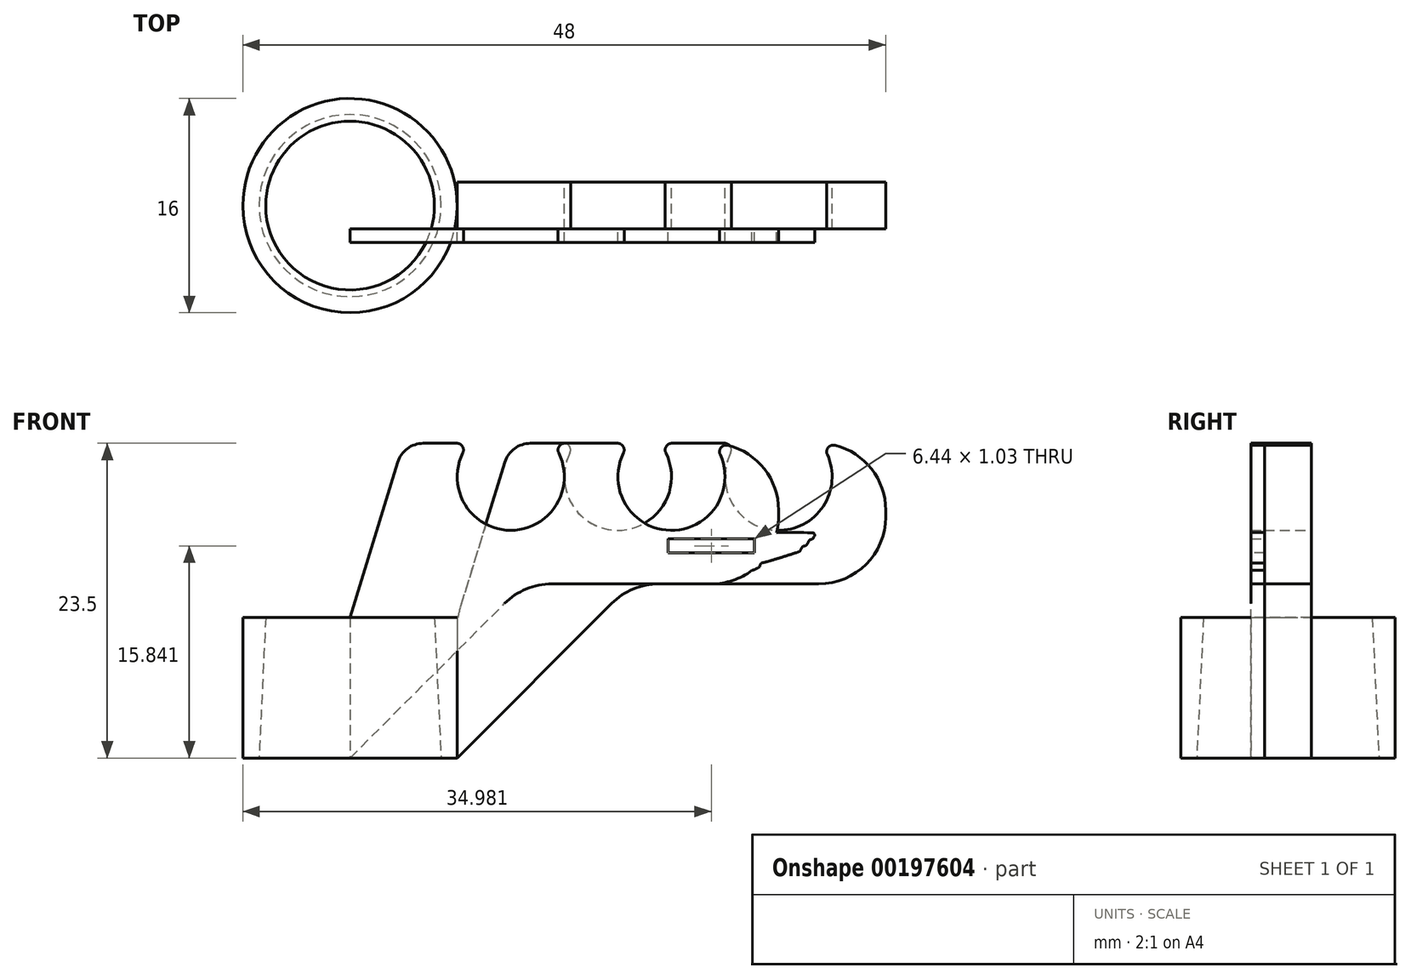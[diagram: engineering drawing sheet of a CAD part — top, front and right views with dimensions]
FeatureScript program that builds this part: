
annotation { "Feature Type Name" : "Feature", "Feature Type Description" : "" }
export const myFeature = defineFeature(function(context is Context, id is Id, definition is map)
    precondition{}
    {
        {
            var Q0;
            Q0=qCreatedBy(makeId("Top.planeOp"),FACE);
            var sketch = newSketch(context, id + "F0", { "sketchPlane" : qUnion([Q0])});
            skCircle(sketch, "E0", {"center": v(0, 0) * mm, "radius": 6.3 * mm});
            skCircle(sketch, "E1", {"center": v(0, 0) * mm, "radius": 8 * mm});
            skCircle(sketch, "E2", {"center": v(0, 0) * mm, "radius": 6.8 * mm});
            skSolve(sketch);
        }
        {
            var Q0;
            Q0=qCreatedBy(makeId("Front.planeOp"),FACE);
            var sketch = newSketch(context, id + "F1", { "sketchPlane" : qUnion([Q0])});
            skLineSegment(sketch, "E3.0", {"start": v(-6.8, 0) * mm, "end": v(6.8, 0) * mm});
            skLineSegment(sketch, "E4.0", {"start": v(-6.3, 0) * mm, "end": v(6.3, 0) * mm});
            skLineSegment(sketch, "E5.0", {"start": v(-8, 0) * mm, "end": v(-5.58, 0) * mm});
            skLineSegment(sketch, "E6", {"start": v(0, 0) * mm, "end": v(0, 10.5) * mm});
            skLineSegment(sketch, "E7.top", {"start": v(-8, 10.5) * mm, "end": v(-6.3, 10.5) * mm});
            skLineSegment(sketch, "E7.left", {"start": v(-8, 0) * mm, "end": v(-8, 10.5) * mm});
            skLineSegment(sketch, "E8", {"start": v(-6.3, 10.5) * mm, "end": v(-6.8, 0) * mm});
            skLineSegment(sketch, "E9.trimOffspring", {"start": v(0, 0) * mm, "end": v(8, 0) * mm});
            skSolve(sketch);
        }
        {
            var Q0;
            Q0=makeQuery(id+"F1.imprint","IMPRINT",FACE,{"disambiguationData":[TD([[makeQuery(id+"F1.imprint","IMPRINT",EDGE,{"derivedFrom":sQuery(id+"F1.wireOp",EDGE,"E7.top")}),-1.0]])]});
            var Q1;
            Q1=sQuery(id+"F1.wireOp",EDGE,"E6");
            revolve(context, id + "F2", {"entities" : qUnion([Q0]), "axis" : qUnion([Q1]), "revolveType" : RevolveType.FULL});
        }
        {
            var Q0;
            Q0=qCreatedBy(makeId("Front.planeOp"),FACE);
            var sketch = newSketch(context, id + "F3", { "sketchPlane" : qUnion([Q0])});
            skLineSegment(sketch, "E10", {"start": v(8, 10.5) * mm, "end": v(8, 0) * mm});
            skLineSegment(sketch, "E11.0", {"start": v(8, 10.5) * mm, "end": v(-8, 10.5) * mm});
            skLineSegment(sketch, "E12.0", {"start": v(-8, 0) * mm, "end": v(8, 0) * mm});
            skLineSegment(sketch, "E13", {"start": v(0, 13) * mm, "end": v(41.13, 13) * mm, "construction": true});
            skLineSegment(sketch, "E14", {"start": v(0, 21) * mm, "end": v(40.48, 21) * mm, "construction": true});
            skLineSegment(sketch, "E15", {"start": v(20, 25.73) * mm, "end": v(20, 4.34) * mm, "construction": true});
            skCircle(sketch, "E16", {"center": v(20, 21) * mm, "radius": 4 * mm});
            skCircle(sketch, "E17.1.0.0", {"center": v(32, 21) * mm, "radius": 4 * mm});
            skLineSegment(sketch, "E17.direction1", {"start": v(20, 21) * mm, "end": v(32, 21) * mm, "construction": true});
            skLineSegment(sketch, "E18", {"start": v(12, 25.64) * mm, "end": v(12, 16.43) * mm, "construction": true});
            skLineSegment(sketch, "E19", {"start": v(12, 23.5) * mm, "end": v(68.02, 23.5) * mm});
            skLineSegment(sketch, "E20", {"start": v(40, 26.61) * mm, "end": v(40, 15.45) * mm, "construction": true});
            skLineSegment(sketch, "E21", {"start": v(12, 23.5) * mm, "end": v(8, 10.5) * mm});
            skLineSegment(sketch, "E22", {"start": v(22.25, 13) * mm, "end": v(41.13, 13) * mm});
            skLineSegment(sketch, "E23", {"start": v(40, 13) * mm, "end": v(40, 23.5) * mm});
            skLineSegment(sketch, "E24", {"start": v(8, 0) * mm, "end": v(21, 13) * mm});
            skPoint(sketch, "E25.orphan", {"position": v(22.25, 14.25) * mm});
            skLineSegment(sketch, "E26", {"start": v(21, 13) * mm, "end": v(22.25, 13) * mm});
            skLineSegment(sketch, "E27", {"start": v(40, 13) * mm, "end": v(41.13, 13) * mm});
            skLineSegment(sketch, "E28.bottom", {"start": v(8, 10.5) * mm, "end": v(7.8, 10.5) * mm});
            skLineSegment(sketch, "E28.top", {"start": v(8, 0) * mm, "end": v(7.8, 0) * mm});
            skLineSegment(sketch, "E28.right", {"start": v(7.8, 10.5) * mm, "end": v(7.8, 0) * mm});
            skSolve(sketch);
        }
        {
            var Q0;
            {var subQ0=sQuery(id+"F3.wireOp",EDGE,"E21");Q0=makeQuery(id+"F3.imprint","IMPRINT",FACE,{"disambiguationData":[TD([[makeQuery(id+"F3.imprint","IMPRINT",EDGE,{"derivedFrom":subQ0}),1.0]])]});}
            var Q1;
            Q1=makeQuery(id+"F3.imprint","IMPRINT",FACE,{"disambiguationData":[TD([[makeQuery(id+"F3.imprint","IMPRINT",EDGE,{"derivedFrom":sQuery(id+"F3.wireOp",EDGE,"E28.bottom")}),1.0]])]});
            extrude(context, id + "F4", {"entities" : qUnion([Q0, Q1]), "operationType" : NewBodyOperationType.ADD, "endBound" : BoundingType.SYMMETRIC, "depth" : 3.5 * mm});
        }
        {
            var Q0;
            Q0=makeQuery(id+"F4.boolean.opBoolean","INTERSECT",EDGE,{"derivedFrom":[makeQuery(id+"F2.opRevolve","SWEPT_FACE",FACE,{"disambiguationData":[OSD([sQuery(id+"F1.wireOp",EDGE,"E7.left")])]}),makeQuery(id+"F4.opExtrude","CAP_FACE",FACE,{"disambiguationData":[OSD([sQuery(id+"F3.wireOp",EDGE,"E16"),sQuery(id+"F3.wireOp",EDGE,"E17.1.0.0"),sQuery(id+"F3.wireOp",EDGE,"E17.2.0.0"),sQuery(id+"F3.wireOp",EDGE,"E17.3.0.0"),sQuery(id+"F3.wireOp",EDGE,"E19"),sQuery(id+"F3.wireOp",EDGE,"E21"),sQuery(id+"F3.wireOp",EDGE,"E22"),sQuery(id+"F3.wireOp",EDGE,"E23"),sQuery(id+"F3.wireOp",EDGE,"E24"),sQuery(id+"F3.wireOp",EDGE,"E26"),sQuery(id+"F3.wireOp",EDGE,"E27"),sQuery(id+"F3.wireOp",EDGE,"E28.bottom"),sQuery(id+"F3.wireOp",EDGE,"E28.top"),sQuery(id+"F3.wireOp",EDGE,"E28.right")])],"isStart":true})]});
            var Q1;
            Q1=makeQuery(id+"F4.boolean.opBoolean","INTERSECT",EDGE,{"derivedFrom":[makeQuery(id+"F2.opRevolve","SWEPT_FACE",FACE,{"disambiguationData":[OSD([sQuery(id+"F1.wireOp",EDGE,"E7.left")])]}),makeQuery(id+"F4.opExtrude","CAP_FACE",FACE,{"disambiguationData":[OSD([sQuery(id+"F3.wireOp",EDGE,"E16"),sQuery(id+"F3.wireOp",EDGE,"E17.1.0.0"),sQuery(id+"F3.wireOp",EDGE,"E17.2.0.0"),sQuery(id+"F3.wireOp",EDGE,"E17.3.0.0"),sQuery(id+"F3.wireOp",EDGE,"E19"),sQuery(id+"F3.wireOp",EDGE,"E21"),sQuery(id+"F3.wireOp",EDGE,"E22"),sQuery(id+"F3.wireOp",EDGE,"E23"),sQuery(id+"F3.wireOp",EDGE,"E24"),sQuery(id+"F3.wireOp",EDGE,"E26"),sQuery(id+"F3.wireOp",EDGE,"E27"),sQuery(id+"F3.wireOp",EDGE,"E28.bottom"),sQuery(id+"F3.wireOp",EDGE,"E28.top"),sQuery(id+"F3.wireOp",EDGE,"E28.right")])],"isStart":false})]});
            var Q2;
            Q2=makeQuery(id+"F4.opExtrude","SWEPT_EDGE",EDGE,{"disambiguationData":[OSD([sQuery(id+"F3.wireOp",EDGE,"E24"),sQuery(id+"F3.wireOp",EDGE,"E26")])]});
            var Q3;
            Q3=makeQuery(id+"F4.opExtrude","SWEPT_EDGE",EDGE,{"disambiguationData":[OSD([sQuery(id+"F3.wireOp",EDGE,"E23"),sQuery(id+"F3.wireOp",EDGE,"E27")])]});
            fillet(context, id + "F5", {"entities" : qUnion([Q0, Q1, Q2, Q3]), "radius" : 5 * mm, "tangentPropagation" : true, "allowEdgeOverflow" : false});
        }
        {
            var Q0;
            Q0=makeQuery(id+"F4.opExtrude","SWEPT_EDGE",EDGE,{"disambiguationData":[OSD([sQuery(id+"F3.wireOp",EDGE,"E19"),sQuery(id+"F3.wireOp",EDGE,"E21")])]});
            var Q1;
            Q1=makeQuery(id+"F4.opExtrude","SWEPT_EDGE",EDGE,{"disambiguationData":[OSD([sQuery(id+"F3.wireOp",EDGE,"E19"),sQuery(id+"F3.wireOp",EDGE,"E23")])]});
            fillet(context, id + "F6", {"entities" : qUnion([Q0, Q1]), "radius" : 2 * mm, "tangentPropagation" : true, "allowEdgeOverflow" : false});
        }
        {
            var Q0;
            {var subQ0=sQuery(id+"F3.wireOp",EDGE,"E19");var subQ1=sQuery(id+"F3.wireOp",EDGE,"E16");Q0=makeQuery(id+"F4.opExtrude","SWEPT_EDGE",EDGE,{"disambiguationData":[OSD([subQ1,subQ0]),TDD([makeQuery(id+"F3.imprint","INTERSECT",VERTEX,{"disambiguationData":[OD(1.0)],"derivedFrom":[subQ1,subQ0]})])]});}
            var Q1;
            {var subQ0=sQuery(id+"F3.wireOp",EDGE,"E19");var subQ1=sQuery(id+"F3.wireOp",EDGE,"E16");Q1=makeQuery(id+"F4.opExtrude","SWEPT_EDGE",EDGE,{"disambiguationData":[OSD([subQ1,subQ0]),TDD([makeQuery(id+"F3.imprint","INTERSECT",VERTEX,{"disambiguationData":[OD(0.0)],"derivedFrom":[subQ1,subQ0]})])]});}
            var Q2;
            {var subQ0=sQuery(id+"F3.wireOp",EDGE,"E19");var subQ1=sQuery(id+"F3.wireOp",EDGE,"E17.1.0.0");Q2=makeQuery(id+"F4.opExtrude","SWEPT_EDGE",EDGE,{"disambiguationData":[OSD([subQ1,subQ0]),TDD([makeQuery(id+"F3.imprint","INTERSECT",VERTEX,{"disambiguationData":[OD(0.0)],"derivedFrom":[subQ1,subQ0]})])]});}
            var Q3;
            {var subQ0=sQuery(id+"F3.wireOp",EDGE,"E19");var subQ1=sQuery(id+"F3.wireOp",EDGE,"E17.2.0.0");Q3=makeQuery(id+"F4.opExtrude","SWEPT_EDGE",EDGE,{"disambiguationData":[OSD([subQ1,subQ0]),TDD([makeQuery(id+"F3.imprint","INTERSECT",VERTEX,{"disambiguationData":[OD(0.0)],"derivedFrom":[subQ1,subQ0]})])]});}
            var Q4;
            {var subQ0=sQuery(id+"F3.wireOp",EDGE,"E19");var subQ1=sQuery(id+"F3.wireOp",EDGE,"E17.3.0.0");Q4=makeQuery(id+"F4.opExtrude","SWEPT_EDGE",EDGE,{"disambiguationData":[OSD([subQ1,subQ0]),TDD([makeQuery(id+"F3.imprint","INTERSECT",VERTEX,{"disambiguationData":[OD(0.0)],"derivedFrom":[subQ1,subQ0]})])]});}
            var Q5;
            {var subQ0=sQuery(id+"F3.wireOp",EDGE,"E19");var subQ1=sQuery(id+"F3.wireOp",EDGE,"E17.1.0.0");Q5=makeQuery(id+"F4.opExtrude","SWEPT_EDGE",EDGE,{"disambiguationData":[OSD([subQ1,subQ0]),TDD([makeQuery(id+"F3.imprint","INTERSECT",VERTEX,{"disambiguationData":[OD(1.0)],"derivedFrom":[subQ1,subQ0]})])]});}
            var Q6;
            {var subQ0=sQuery(id+"F3.wireOp",EDGE,"E19");var subQ1=sQuery(id+"F3.wireOp",EDGE,"E17.2.0.0");Q6=makeQuery(id+"F4.opExtrude","SWEPT_EDGE",EDGE,{"disambiguationData":[OSD([subQ1,subQ0]),TDD([makeQuery(id+"F3.imprint","INTERSECT",VERTEX,{"disambiguationData":[OD(1.0)],"derivedFrom":[subQ1,subQ0]})])]});}
            var Q7;
            {var subQ0=sQuery(id+"F3.wireOp",EDGE,"E19");var subQ1=sQuery(id+"F3.wireOp",EDGE,"E17.3.0.0");Q7=makeQuery(id+"F4.opExtrude","SWEPT_EDGE",EDGE,{"disambiguationData":[OSD([subQ1,subQ0]),TDD([makeQuery(id+"F3.imprint","INTERSECT",VERTEX,{"disambiguationData":[OD(1.0)],"derivedFrom":[subQ1,subQ0]})])]});}
            var Q8;
            Q8=makeQuery(id+"F5.opFillet","BLEND_EDGE",EDGE,{"blendedFrom":[makeQuery(id+"F4.opExtrude","SWEPT_EDGE",EDGE,{"disambiguationData":[OSD([sQuery(id+"F3.wireOp",EDGE,"E19"),sQuery(id+"F3.wireOp",EDGE,"E23")])]}),makeQuery(id+"F4.opExtrude","SWEPT_FACE",FACE,{"disambiguationData":[OSD([sQuery(id+"F3.wireOp",EDGE,"E17.1.0.0")])]})],"blendedInto":[makeQuery(id+"F4.opExtrude","SWEPT_FACE",FACE,{"disambiguationData":[OSD([sQuery(id+"F3.wireOp",EDGE,"E17.1.0.0")])]})]});
            fillet(context, id + "F7", {"entities" : qUnion([Q0, Q1, Q2, Q3, Q4, Q5, Q6, Q7, Q8]), "radius" : .5 * mm, "tangentPropagation" : true, "allowEdgeOverflow" : false});
        }
        {
            var Q0;
            Q0=makeQuery(id+"F4.opExtrude","CAP_FACE",FACE,{"disambiguationData":[OSD([sQuery(id+"F3.wireOp",EDGE,"E16"),sQuery(id+"F3.wireOp",EDGE,"E17.1.0.0"),sQuery(id+"F3.wireOp",EDGE,"E17.2.0.0"),sQuery(id+"F3.wireOp",EDGE,"E17.3.0.0"),sQuery(id+"F3.wireOp",EDGE,"E19"),sQuery(id+"F3.wireOp",EDGE,"E21"),sQuery(id+"F3.wireOp",EDGE,"E22"),sQuery(id+"F3.wireOp",EDGE,"E23"),sQuery(id+"F3.wireOp",EDGE,"E24"),sQuery(id+"F3.wireOp",EDGE,"E26"),sQuery(id+"F3.wireOp",EDGE,"E27"),sQuery(id+"F3.wireOp",EDGE,"E28.bottom"),sQuery(id+"F3.wireOp",EDGE,"E28.top"),sQuery(id+"F3.wireOp",EDGE,"E28.right")])],"isStart":false});
            var sketch = newSketch(context, id + "F8", { "sketchPlane" : qUnion([Q0])});
            skFitSpline(sketch, "E29", {"points": [v(35.71, 16.35) * mm, v(35.78, 16.55) * mm, v(35.85, 16.65) * mm, v(35.98, 16.75) * mm, v(36.12, 16.8) * mm, v(36.24, 16.8) * mm, v(42.55, 16.82) * mm, v(42.65, 16.78) * mm, v(42.7, 16.65) * mm, v(42.65, 16.52) * mm, v(42.55, 16.36) * mm, v(42.42, 16.32) * mm, v(42.3, 16.26) * mm, v(42.08, 15.9) * mm, v(41.89, 15.83) * mm, v(41.78, 15.76) * mm, v(41.62, 15.48) * mm, v(41.45, 15.38) * mm, v(38.77, 14.57) * mm, v(38.7, 14.56) * mm, v(38.62, 14.38) * mm, v(38.56, 14.27) * mm, v(38.18, 14.06) * mm, v(38.06, 14.02) * mm, v(35.9, 13.44) * mm, v(35.75, 13.44) * mm, v(35.65, 13.48) * mm, v(35.59, 13.53) * mm, v(35, 14.06) * mm, v(34.97, 14.05) * mm, v(34.9, 14.03) * mm, v(34.85, 14) * mm, v(34.31, 13.47) * mm, v(34.24, 13.44) * mm, v(34.16, 13.44) * mm, v(31.77, 14.07) * mm, v(31.41, 14.28) * mm, v(31.3, 14.48) * mm, v(31.22, 14.57) * mm, v(31.12, 14.6) * mm, v(28.44, 15.4) * mm, v(28.33, 15.52) * mm, v(28.2, 15.88) * mm, v(28.14, 15.83) * mm, v(28.02, 15.85) * mm, v(27.94, 15.87) * mm, v(27.88, 15.92) * mm, v(27.69, 16.27) * mm, v(27.65, 16.3) * mm, v(27.51, 16.3) * mm, v(27.46, 16.32) * mm, v(27.28, 16.62) * mm, v(27.28, 16.7) * mm, v(27.33, 16.77) * mm, v(27.4, 16.8) * mm, v(27.46, 16.8) * mm, v(33.8, 16.81) * mm, v(33.85, 16.81) * mm, v(33.97, 16.77) * mm, v(34.17, 16.6) * mm, v(34.2, 16.5) * mm, v(34.25, 16.4) * mm, v(34.26, 16.34) * mm, v(34.33, 16.34) * mm, v(35.58, 16.34) * mm, v(35.71, 16.35) * mm]});
            skFitSpline(sketch, "E30", {"points": [v(30.68, 16.8) * mm, v(30.83, 16.69) * mm, v(30.9, 16.62) * mm, v(30.99, 16.5) * mm, v(31.06, 16.33) * mm, v(31.28, 16.02) * mm, v(31.53, 15.67) * mm, v(31.6, 15.6) * mm, v(32.13, 15.09) * mm, v(32.73, 14.67) * mm, v(33.36, 14.37) * mm, v(33.87, 14.2) * mm, v(34.55, 14.1) * mm, v(35, 14.06) * mm, v(35.61, 14.1) * mm, v(36.24, 14.24) * mm, v(36.81, 14.44) * mm, v(37.3, 14.7) * mm, v(37.8, 15.05) * mm, v(38.1, 15.33) * mm, v(38.48, 15.75) * mm, v(38.72, 16.05) * mm, v(38.93, 16.39) * mm, v(39.08, 16.63) * mm, v(39.22, 16.76) * mm, v(39.4, 16.82) * mm, v(39.46, 16.82) * mm], "startDerivative": vector(6.61, -4.14) * mm, "endDerivative": vector(2.94, -0.27) * mm});
            skLineSegment(sketch, "E31.bottom", {"start": v(31.76, 16.35) * mm, "end": v(38.2, 16.35) * mm});
            skLineSegment(sketch, "E31.top", {"start": v(31.76, 15.33) * mm, "end": v(38.2, 15.33) * mm});
            skLineSegment(sketch, "E31.left", {"start": v(31.76, 16.35) * mm, "end": v(31.76, 15.33) * mm});
            skLineSegment(sketch, "E31.right", {"start": v(38.2, 16.35) * mm, "end": v(38.2, 15.33) * mm});
            skLineSegment(sketch, "E32", {"start": v(27.69, 16.27) * mm, "end": v(31.76, 16.35) * mm});
            skLineSegment(sketch, "E33", {"start": v(31.76, 16.1) * mm, "end": v(28.2, 15.88) * mm});
            skLineSegment(sketch, "E34", {"start": v(31.76, 15.88) * mm, "end": v(28.44, 15.4) * mm});
            skLineSegment(sketch, "E35", {"start": v(31.76, 15.67) * mm, "end": v(29.25, 15.15) * mm});
            skLineSegment(sketch, "E36", {"start": v(31.76, 15.33) * mm, "end": v(30.28, 14.84) * mm});
            skLineSegment(sketch, "E37", {"start": v(32.82, 15.33) * mm, "end": v(31.22, 14.57) * mm});
            skLineSegment(sketch, "E38", {"start": v(33.59, 15.33) * mm, "end": v(31.77, 14.07) * mm});
            skLineSegment(sketch, "E39", {"start": v(34.05, 15.33) * mm, "end": v(32.59, 13.83) * mm});
            skLineSegment(sketch, "E40", {"start": v(34.4, 15.33) * mm, "end": v(33.39, 13.61) * mm});
            skLineSegment(sketch, "E41", {"start": v(34.73, 15.33) * mm, "end": v(34.16, 13.44) * mm});
            skLineSegment(sketch, "E42", {"start": v(34.98, 15.33) * mm, "end": v(34.97, 14.05) * mm});
            skLineSegment(sketch, "E43", {"start": v(35.26, 15.33) * mm, "end": v(35.81, 13.43) * mm});
            skLineSegment(sketch, "E44", {"start": v(35.61, 15.33) * mm, "end": v(36.58, 13.6) * mm});
            skLineSegment(sketch, "E45", {"start": v(35.96, 15.33) * mm, "end": v(37.37, 13.83) * mm});
            skLineSegment(sketch, "E46", {"start": v(36.38, 15.33) * mm, "end": v(38.18, 14.06) * mm});
            skLineSegment(sketch, "E47", {"start": v(37.14, 15.33) * mm, "end": v(38.77, 14.57) * mm});
            skLineSegment(sketch, "E48", {"start": v(38.2, 15.33) * mm, "end": v(39.77, 14.85) * mm});
            skLineSegment(sketch, "E49", {"start": v(38.2, 15.65) * mm, "end": v(40.68, 15.13) * mm});
            skLineSegment(sketch, "E50", {"start": v(38.2, 15.87) * mm, "end": v(41.57, 15.43) * mm});
            skLineSegment(sketch, "E51", {"start": v(38.2, 16.1) * mm, "end": v(42.02, 15.86) * mm});
            skLineSegment(sketch, "E52", {"start": v(38.2, 16.3) * mm, "end": v(42.35, 16.3) * mm});
            skSolve(sketch);
        }
        {
            var Q0;
            {var subQ5=sQuery(id+"F8.wireOp",EDGE,"E36");Q0=makeQuery(id+"F8.imprint","IMPRINT",FACE,{"disambiguationData":[TD([[makeQuery(id+"F8.imprint","IMPRINT",EDGE,{"derivedFrom":subQ5}),-1.0]])]});}
            var Q1;
            {var subQ0=sQuery(id+"F8.wireOp",EDGE,"E46");var subQ1=sQuery(id+"F8.wireOp",EDGE,"E29");var subQ2=makeQuery(id+"F8.imprint","INTERSECT",VERTEX,{"derivedFrom":[subQ1,subQ0]});Q1=makeQuery(id+"F8.imprint","IMPRINT",FACE,{"disambiguationData":[TD([[makeQuery(id+"F8.imprint","IMPRINT",EDGE,{"disambiguationData":[TD([[subQ2,1.0]])],"derivedFrom":subQ1}),-1.0]])]});}
            var Q2;
            {var subQ0=sQuery(id+"F8.wireOp",EDGE,"E38");var subQ1=sQuery(id+"F8.wireOp",EDGE,"E29");var subQ2=makeQuery(id+"F8.imprint","INTERSECT",VERTEX,{"derivedFrom":[subQ1,subQ0]});Q2=makeQuery(id+"F8.imprint","IMPRINT",FACE,{"disambiguationData":[TD([[makeQuery(id+"F8.imprint","IMPRINT",EDGE,{"disambiguationData":[TD([[subQ2,1.0]])],"derivedFrom":subQ1}),-1.0]])]});}
            var Q3;
            {var subQ0=sQuery(id+"F8.wireOp",EDGE,"E44");var subQ1=sQuery(id+"F8.wireOp",EDGE,"E30");var subQ2=makeQuery(id+"F8.imprint","INTERSECT",VERTEX,{"derivedFrom":[subQ1,subQ0]});Q3=makeQuery(id+"F8.imprint","IMPRINT",FACE,{"disambiguationData":[TD([[makeQuery(id+"F8.imprint","IMPRINT",EDGE,{"disambiguationData":[TD([[subQ2,-1.0]])],"derivedFrom":subQ1}),1.0]])]});}
            var Q4;
            {var subQ0=sQuery(id+"F8.wireOp",EDGE,"E39");var subQ1=sQuery(id+"F8.wireOp",EDGE,"E29");var subQ2=makeQuery(id+"F8.imprint","INTERSECT",VERTEX,{"derivedFrom":[subQ1,subQ0]});Q4=makeQuery(id+"F8.imprint","IMPRINT",FACE,{"disambiguationData":[TD([[makeQuery(id+"F8.imprint","IMPRINT",EDGE,{"disambiguationData":[TD([[subQ2,1.0]])],"derivedFrom":subQ1}),-1.0]])]});}
            var Q5;
            {var subQ0=sQuery(id+"F8.wireOp",EDGE,"E43");var subQ1=sQuery(id+"F8.wireOp",EDGE,"E30");var subQ2=makeQuery(id+"F8.imprint","INTERSECT",VERTEX,{"derivedFrom":[subQ1,subQ0]});Q5=makeQuery(id+"F8.imprint","IMPRINT",FACE,{"disambiguationData":[TD([[makeQuery(id+"F8.imprint","IMPRINT",EDGE,{"disambiguationData":[TD([[subQ2,-1.0]])],"derivedFrom":subQ1}),1.0]])]});}
            var Q6;
            {var subQ0=sQuery(id+"F8.wireOp",EDGE,"E30");var subQ1=sQuery(id+"F8.wireOp",EDGE,"E29");var subQ2=makeQuery(id+"F8.imprint","INTERSECT",VERTEX,{"disambiguationData":[OD(0.0)],"derivedFrom":[subQ1,subQ0]});Q6=makeQuery(id+"F8.imprint","IMPRINT",FACE,{"disambiguationData":[TD([[makeQuery(id+"F8.imprint","IMPRINT",EDGE,{"disambiguationData":[TD([[subQ2,-1.0]])],"derivedFrom":subQ1}),-1.0]])]});}
            var Q7;
            {var subQ0=sQuery(id+"F8.wireOp",EDGE,"E41");var subQ1=sQuery(id+"F8.wireOp",EDGE,"E30");var subQ2=makeQuery(id+"F8.imprint","INTERSECT",VERTEX,{"derivedFrom":[subQ1,subQ0]});Q7=makeQuery(id+"F8.imprint","IMPRINT",FACE,{"disambiguationData":[TD([[makeQuery(id+"F8.imprint","IMPRINT",EDGE,{"disambiguationData":[TD([[subQ2,-1.0]])],"derivedFrom":subQ1}),1.0]])]});}
            var Q8;
            {var subQ0=sQuery(id+"F8.wireOp",EDGE,"E32");var subQ1=sQuery(id+"F8.wireOp",EDGE,"E30");var subQ2=makeQuery(id+"F8.imprint","INTERSECT",VERTEX,{"derivedFrom":[subQ1,subQ0]});Q8=makeQuery(id+"F8.imprint","IMPRINT",FACE,{"disambiguationData":[TD([[makeQuery(id+"F8.imprint","IMPRINT",EDGE,{"disambiguationData":[TD([[subQ2,-1.0]])],"derivedFrom":subQ1}),1.0]])]});}
            var Q9;
            {var subQ0=sQuery(id+"F8.wireOp",EDGE,"E47");var subQ1=sQuery(id+"F8.wireOp",EDGE,"E29");var subQ2=makeQuery(id+"F8.imprint","INTERSECT",VERTEX,{"derivedFrom":[subQ1,subQ0]});Q9=makeQuery(id+"F8.imprint","IMPRINT",FACE,{"disambiguationData":[TD([[makeQuery(id+"F8.imprint","IMPRINT",EDGE,{"disambiguationData":[TD([[subQ2,1.0]])],"derivedFrom":subQ1}),-1.0]])]});}
            var Q10;
            {var subQ0=sQuery(id+"F8.wireOp",EDGE,"E32");var subQ1=sQuery(id+"F8.wireOp",EDGE,"E29");var subQ2=makeQuery(id+"F8.imprint","INTERSECT",VERTEX,{"derivedFrom":[subQ1,subQ0]});Q10=makeQuery(id+"F8.imprint","IMPRINT",FACE,{"disambiguationData":[TD([[makeQuery(id+"F8.imprint","IMPRINT",EDGE,{"disambiguationData":[TD([[subQ2,1.0]])],"derivedFrom":subQ1}),-1.0]])]});}
            var Q11;
            {var subQ0=sQuery(id+"F8.wireOp",EDGE,"E40");var subQ1=sQuery(id+"F8.wireOp",EDGE,"E30");var subQ2=makeQuery(id+"F8.imprint","INTERSECT",VERTEX,{"derivedFrom":[subQ1,subQ0]});Q11=makeQuery(id+"F8.imprint","IMPRINT",FACE,{"disambiguationData":[TD([[makeQuery(id+"F8.imprint","IMPRINT",EDGE,{"disambiguationData":[TD([[subQ2,-1.0]])],"derivedFrom":subQ1}),1.0]])]});}
            var Q12;
            {var subQ3=sQuery(id+"F8.wireOp",EDGE,"E29");var subQ7=sQuery(id+"F8.wireOp",EDGE,"E30");var subQ8=makeQuery(id+"F8.imprint","INTERSECT",VERTEX,{"disambiguationData":[OD(2.0)],"derivedFrom":[subQ3,subQ7]});Q12=makeQuery(id+"F8.imprint","IMPRINT",FACE,{"disambiguationData":[TD([[makeQuery(id+"F8.imprint","IMPRINT",EDGE,{"disambiguationData":[TD([[subQ8,1.0]])],"derivedFrom":subQ3}),-1.0]])]});}
            var Q13;
            {var subQ0=sQuery(id+"F8.wireOp",EDGE,"E48");var subQ1=sQuery(id+"F8.wireOp",EDGE,"E29");var subQ2=makeQuery(id+"F8.imprint","INTERSECT",VERTEX,{"derivedFrom":[subQ1,subQ0]});Q13=makeQuery(id+"F8.imprint","IMPRINT",FACE,{"disambiguationData":[TD([[makeQuery(id+"F8.imprint","IMPRINT",EDGE,{"disambiguationData":[TD([[subQ2,1.0]])],"derivedFrom":subQ1}),-1.0]])]});}
            var Q14;
            {var subQ0=sQuery(id+"F8.wireOp",EDGE,"E33");var subQ1=sQuery(id+"F8.wireOp",EDGE,"E29");var subQ2=makeQuery(id+"F8.imprint","INTERSECT",VERTEX,{"derivedFrom":[subQ1,subQ0]});Q14=makeQuery(id+"F8.imprint","IMPRINT",FACE,{"disambiguationData":[TD([[makeQuery(id+"F8.imprint","IMPRINT",EDGE,{"disambiguationData":[TD([[subQ2,1.0]])],"derivedFrom":subQ1}),-1.0]])]});}
            var Q15;
            {var subQ0=sQuery(id+"F8.wireOp",EDGE,"E39");var subQ1=sQuery(id+"F8.wireOp",EDGE,"E30");var subQ2=makeQuery(id+"F8.imprint","INTERSECT",VERTEX,{"derivedFrom":[subQ1,subQ0]});Q15=makeQuery(id+"F8.imprint","IMPRINT",FACE,{"disambiguationData":[TD([[makeQuery(id+"F8.imprint","IMPRINT",EDGE,{"disambiguationData":[TD([[subQ2,-1.0]])],"derivedFrom":subQ1}),1.0]])]});}
            var Q16;
            {var subQ0=sQuery(id+"F8.wireOp",EDGE,"E34");var subQ1=sQuery(id+"F8.wireOp",EDGE,"E29");var subQ2=makeQuery(id+"F8.imprint","INTERSECT",VERTEX,{"derivedFrom":[subQ1,subQ0]});Q16=makeQuery(id+"F8.imprint","IMPRINT",FACE,{"disambiguationData":[TD([[makeQuery(id+"F8.imprint","IMPRINT",EDGE,{"disambiguationData":[TD([[subQ2,1.0]])],"derivedFrom":subQ1}),-1.0]])]});}
            var Q17;
            {var subQ0=sQuery(id+"F8.wireOp",EDGE,"E46");var subQ1=sQuery(id+"F8.wireOp",EDGE,"E30");var subQ2=makeQuery(id+"F8.imprint","INTERSECT",VERTEX,{"derivedFrom":[subQ1,subQ0]});Q17=makeQuery(id+"F8.imprint","IMPRINT",FACE,{"disambiguationData":[TD([[makeQuery(id+"F8.imprint","IMPRINT",EDGE,{"disambiguationData":[TD([[subQ2,-1.0]])],"derivedFrom":subQ1}),1.0]])]});}
            var Q18;
            {var subQ0=sQuery(id+"F8.wireOp",EDGE,"E38");var subQ1=sQuery(id+"F8.wireOp",EDGE,"E30");var subQ2=makeQuery(id+"F8.imprint","INTERSECT",VERTEX,{"derivedFrom":[subQ1,subQ0]});Q18=makeQuery(id+"F8.imprint","IMPRINT",FACE,{"disambiguationData":[TD([[makeQuery(id+"F8.imprint","IMPRINT",EDGE,{"disambiguationData":[TD([[subQ2,-1.0]])],"derivedFrom":subQ1}),1.0]])]});}
            var Q19;
            {var subQ0=sQuery(id+"F8.wireOp",EDGE,"E36");Q19=makeQuery(id+"F8.imprint","IMPRINT",FACE,{"disambiguationData":[TD([[makeQuery(id+"F8.imprint","IMPRINT",EDGE,{"derivedFrom":subQ0}),1.0]])]});}
            var Q20;
            {var subQ0=sQuery(id+"F8.wireOp",EDGE,"E44");var subQ1=sQuery(id+"F8.wireOp",EDGE,"E29");var subQ2=makeQuery(id+"F8.imprint","INTERSECT",VERTEX,{"derivedFrom":[subQ1,subQ0]});Q20=makeQuery(id+"F8.imprint","IMPRINT",FACE,{"disambiguationData":[TD([[makeQuery(id+"F8.imprint","IMPRINT",EDGE,{"disambiguationData":[TD([[subQ2,1.0]])],"derivedFrom":subQ1}),-1.0]])]});}
            var Q21;
            {var subQ0=sQuery(id+"F8.wireOp",EDGE,"E37");var subQ1=sQuery(id+"F8.wireOp",EDGE,"E30");var subQ2=makeQuery(id+"F8.imprint","INTERSECT",VERTEX,{"derivedFrom":[subQ1,subQ0]});Q21=makeQuery(id+"F8.imprint","IMPRINT",FACE,{"disambiguationData":[TD([[makeQuery(id+"F8.imprint","IMPRINT",EDGE,{"disambiguationData":[TD([[subQ2,-1.0]])],"derivedFrom":subQ1}),1.0]])]});}
            var Q22;
            {var subQ5=sQuery(id+"F8.wireOp",EDGE,"E30");var subQ6=sQuery(id+"F8.wireOp",EDGE,"E29");var subQ9=makeQuery(id+"F8.imprint","INTERSECT",VERTEX,{"disambiguationData":[OD(3.0)],"derivedFrom":[subQ6,subQ5]});Q22=makeQuery(id+"F8.imprint","IMPRINT",FACE,{"disambiguationData":[TD([[makeQuery(id+"F8.imprint","IMPRINT",EDGE,{"disambiguationData":[TD([[subQ9,-1.0]])],"derivedFrom":subQ6}),-1.0]])]});}
            var Q23;
            {var subQ1=sQuery(id+"F8.wireOp",EDGE,"E30");var subQ7=sQuery(id+"F8.wireOp",EDGE,"E45");var subQ10=makeQuery(id+"F8.imprint","INTERSECT",VERTEX,{"derivedFrom":[subQ1,subQ7]});Q23=makeQuery(id+"F8.imprint","IMPRINT",FACE,{"disambiguationData":[TD([[makeQuery(id+"F8.imprint","IMPRINT",EDGE,{"disambiguationData":[TD([[subQ10,-1.0]])],"derivedFrom":subQ1}),-1.0]])]});}
            var Q24;
            {var subQ1=sQuery(id+"F8.wireOp",EDGE,"E30");var subQ7=sQuery(id+"F8.wireOp",EDGE,"E29");var subQ10=makeQuery(id+"F8.imprint","INTERSECT",VERTEX,{"disambiguationData":[OD(1.0)],"derivedFrom":[subQ7,subQ1]});Q24=makeQuery(id+"F8.imprint","IMPRINT",FACE,{"disambiguationData":[TD([[makeQuery(id+"F8.imprint","IMPRINT",EDGE,{"disambiguationData":[TD([[subQ10,1.0]])],"derivedFrom":subQ7}),-1.0]])]});}
            var Q25;
            {var subQ0=sQuery(id+"F8.wireOp",EDGE,"E47");var subQ1=sQuery(id+"F8.wireOp",EDGE,"E30");var subQ2=makeQuery(id+"F8.imprint","INTERSECT",VERTEX,{"derivedFrom":[subQ1,subQ0]});Q25=makeQuery(id+"F8.imprint","IMPRINT",FACE,{"disambiguationData":[TD([[makeQuery(id+"F8.imprint","IMPRINT",EDGE,{"disambiguationData":[TD([[subQ2,-1.0]])],"derivedFrom":subQ1}),1.0]])]});}
            var Q26;
            {var subQ0=sQuery(id+"F8.wireOp",EDGE,"E37");var subQ1=sQuery(id+"F8.wireOp",EDGE,"E29");var subQ2=makeQuery(id+"F8.imprint","INTERSECT",VERTEX,{"derivedFrom":[subQ1,subQ0]});Q26=makeQuery(id+"F8.imprint","IMPRINT",FACE,{"disambiguationData":[TD([[makeQuery(id+"F8.imprint","IMPRINT",EDGE,{"disambiguationData":[TD([[subQ2,1.0]])],"derivedFrom":subQ1}),-1.0]])]});}
            var Q27;
            {var subQ0=sQuery(id+"F8.wireOp",EDGE,"E45");var subQ1=sQuery(id+"F8.wireOp",EDGE,"E30");var subQ2=makeQuery(id+"F8.imprint","INTERSECT",VERTEX,{"derivedFrom":[subQ1,subQ0]});Q27=makeQuery(id+"F8.imprint","IMPRINT",FACE,{"disambiguationData":[TD([[makeQuery(id+"F8.imprint","IMPRINT",EDGE,{"disambiguationData":[TD([[subQ2,-1.0]])],"derivedFrom":subQ1}),1.0]])]});}
            var Q28;
            {var subQ0=sQuery(id+"F8.wireOp",EDGE,"E30");var subQ1=sQuery(id+"F8.wireOp",EDGE,"E29");var subQ2=makeQuery(id+"F8.imprint","INTERSECT",VERTEX,{"disambiguationData":[OD(0.0)],"derivedFrom":[subQ1,subQ0]});Q28=makeQuery(id+"F8.imprint","IMPRINT",FACE,{"disambiguationData":[TD([[makeQuery(id+"F8.imprint","IMPRINT",EDGE,{"disambiguationData":[TD([[subQ2,1.0]])],"derivedFrom":subQ1}),-1.0]])]});}
            var Q29;
            {var subQ0=sQuery(id+"F8.wireOp",EDGE,"E31.bottom");var subQ1=sQuery(id+"F8.wireOp",EDGE,"E29");var subQ2=makeQuery(id+"F8.imprint","INTERSECT",VERTEX,{"disambiguationData":[OD(0.0)],"derivedFrom":[subQ1,subQ0]});Q29=makeQuery(id+"F8.imprint","IMPRINT",FACE,{"disambiguationData":[TD([[makeQuery(id+"F8.imprint","IMPRINT",EDGE,{"disambiguationData":[TD([[subQ2,-1.0]])],"derivedFrom":subQ1}),1.0]])]});}
            var Q30;
            {var subQ0=sQuery(id+"F8.wireOp",EDGE,"E50");var subQ1=sQuery(id+"F8.wireOp",EDGE,"E29");var subQ2=makeQuery(id+"F8.imprint","INTERSECT",VERTEX,{"derivedFrom":[subQ1,subQ0]});Q30=makeQuery(id+"F8.imprint","IMPRINT",FACE,{"disambiguationData":[TD([[makeQuery(id+"F8.imprint","IMPRINT",EDGE,{"disambiguationData":[TD([[subQ2,1.0]])],"derivedFrom":subQ1}),-1.0]])]});}
            var Q31;
            {var subQ0=sQuery(id+"F8.wireOp",EDGE,"E51");var subQ1=sQuery(id+"F8.wireOp",EDGE,"E29");var subQ2=makeQuery(id+"F8.imprint","INTERSECT",VERTEX,{"derivedFrom":[subQ1,subQ0]});Q31=makeQuery(id+"F8.imprint","IMPRINT",FACE,{"disambiguationData":[TD([[makeQuery(id+"F8.imprint","IMPRINT",EDGE,{"disambiguationData":[TD([[subQ2,1.0]])],"derivedFrom":subQ1}),-1.0]])]});}
            var Q32;
            {var subQ0=sQuery(id+"F8.wireOp",EDGE,"E49");var subQ1=sQuery(id+"F8.wireOp",EDGE,"E29");var subQ2=makeQuery(id+"F8.imprint","INTERSECT",VERTEX,{"derivedFrom":[subQ1,subQ0]});Q32=makeQuery(id+"F8.imprint","IMPRINT",FACE,{"disambiguationData":[TD([[makeQuery(id+"F8.imprint","IMPRINT",EDGE,{"disambiguationData":[TD([[subQ2,1.0]])],"derivedFrom":subQ1}),-1.0]])]});}
            var Q33;
            {var subQ0=sQuery(id+"F8.wireOp",EDGE,"E51");var subQ1=sQuery(id+"F8.wireOp",EDGE,"E30");var subQ2=makeQuery(id+"F8.imprint","INTERSECT",VERTEX,{"derivedFrom":[subQ1,subQ0]});Q33=makeQuery(id+"F8.imprint","IMPRINT",FACE,{"disambiguationData":[TD([[makeQuery(id+"F8.imprint","IMPRINT",EDGE,{"disambiguationData":[TD([[subQ2,-1.0]])],"derivedFrom":subQ1}),1.0]])]});}
            var Q34;
            {var subQ0=sQuery(id+"F8.wireOp",EDGE,"E50");var subQ1=sQuery(id+"F8.wireOp",EDGE,"E30");var subQ2=makeQuery(id+"F8.imprint","INTERSECT",VERTEX,{"derivedFrom":[subQ1,subQ0]});Q34=makeQuery(id+"F8.imprint","IMPRINT",FACE,{"disambiguationData":[TD([[makeQuery(id+"F8.imprint","IMPRINT",EDGE,{"disambiguationData":[TD([[subQ2,-1.0]])],"derivedFrom":subQ1}),1.0]])]});}
            var Q35;
            {var subQ0=sQuery(id+"F8.wireOp",EDGE,"E49");var subQ1=sQuery(id+"F8.wireOp",EDGE,"E30");var subQ2=makeQuery(id+"F8.imprint","INTERSECT",VERTEX,{"derivedFrom":[subQ1,subQ0]});Q35=makeQuery(id+"F8.imprint","IMPRINT",FACE,{"disambiguationData":[TD([[makeQuery(id+"F8.imprint","IMPRINT",EDGE,{"disambiguationData":[TD([[subQ2,-1.0]])],"derivedFrom":subQ1}),1.0]])]});}
            var Q36;
            {var subQ0=sQuery(id+"F8.wireOp",EDGE,"E33");var subQ1=sQuery(id+"F8.wireOp",EDGE,"E30");var subQ2=makeQuery(id+"F8.imprint","INTERSECT",VERTEX,{"derivedFrom":[subQ1,subQ0]});Q36=makeQuery(id+"F8.imprint","IMPRINT",FACE,{"disambiguationData":[TD([[makeQuery(id+"F8.imprint","IMPRINT",EDGE,{"disambiguationData":[TD([[subQ2,-1.0]])],"derivedFrom":subQ1}),1.0]])]});}
            var Q37;
            {var subQ0=sQuery(id+"F8.wireOp",EDGE,"E31.top");var subQ1=sQuery(id+"F8.wireOp",EDGE,"E30");var subQ2=makeQuery(id+"F8.imprint","INTERSECT",VERTEX,{"disambiguationData":[OD(0.0)],"derivedFrom":[subQ1,subQ0]});Q37=makeQuery(id+"F8.imprint","IMPRINT",FACE,{"disambiguationData":[TD([[makeQuery(id+"F8.imprint","IMPRINT",EDGE,{"disambiguationData":[TD([[subQ2,-1.0]])],"derivedFrom":subQ1}),1.0]])]});}
            var Q38;
            {var subQ0=sQuery(id+"F8.wireOp",EDGE,"E34");var subQ1=sQuery(id+"F8.wireOp",EDGE,"E30");var subQ2=makeQuery(id+"F8.imprint","INTERSECT",VERTEX,{"derivedFrom":[subQ1,subQ0]});Q38=makeQuery(id+"F8.imprint","IMPRINT",FACE,{"disambiguationData":[TD([[makeQuery(id+"F8.imprint","IMPRINT",EDGE,{"disambiguationData":[TD([[subQ2,-1.0]])],"derivedFrom":subQ1}),1.0]])]});}
            var Q39;
            {var subQ0=sQuery(id+"F8.wireOp",EDGE,"E31.right");var subQ1=sQuery(id+"F8.wireOp",EDGE,"E30");var subQ2=makeQuery(id+"F8.imprint","INTERSECT",VERTEX,{"derivedFrom":[subQ1,subQ0]});Q39=makeQuery(id+"F8.imprint","IMPRINT",FACE,{"disambiguationData":[TD([[makeQuery(id+"F8.imprint","IMPRINT",EDGE,{"disambiguationData":[TD([[subQ2,-1.0]])],"derivedFrom":subQ1}),1.0]])]});}
            var Q40;
            {var subQ0=sQuery(id+"F8.wireOp",EDGE,"E35");var subQ1=sQuery(id+"F8.wireOp",EDGE,"E30");var subQ2=makeQuery(id+"F8.imprint","INTERSECT",VERTEX,{"derivedFrom":[subQ1,subQ0]});Q40=makeQuery(id+"F8.imprint","IMPRINT",FACE,{"disambiguationData":[TD([[makeQuery(id+"F8.imprint","IMPRINT",EDGE,{"disambiguationData":[TD([[subQ2,-1.0]])],"derivedFrom":subQ1}),1.0]])]});}
            var Q41;
            {var subQ0=sQuery(id+"F8.wireOp",EDGE,"E30");var subQ1=sQuery(id+"F8.wireOp",EDGE,"E29");var subQ2=makeQuery(id+"F8.imprint","INTERSECT",VERTEX,{"disambiguationData":[OD(1.0)],"derivedFrom":[subQ1,subQ0]});Q41=makeQuery(id+"F8.imprint","IMPRINT",FACE,{"disambiguationData":[TD([[makeQuery(id+"F8.imprint","IMPRINT",EDGE,{"disambiguationData":[TD([[subQ2,1.0]])],"derivedFrom":subQ1}),1.0]])]});}
            var Q42;
            {var subQ0=sQuery(id+"F8.wireOp",EDGE,"E31.top");var subQ1=sQuery(id+"F8.wireOp",EDGE,"E30");var subQ2=makeQuery(id+"F8.imprint","INTERSECT",VERTEX,{"disambiguationData":[OD(1.0)],"derivedFrom":[subQ1,subQ0]});Q42=makeQuery(id+"F8.imprint","IMPRINT",FACE,{"disambiguationData":[TD([[makeQuery(id+"F8.imprint","IMPRINT",EDGE,{"disambiguationData":[TD([[subQ2,-1.0]])],"derivedFrom":subQ1}),-1.0]])]});}
            var Q43;
            {var subQ0=sQuery(id+"F8.wireOp",EDGE,"E31.left");var subQ1=sQuery(id+"F8.wireOp",EDGE,"E30");var subQ2=makeQuery(id+"F8.imprint","INTERSECT",VERTEX,{"derivedFrom":[subQ1,subQ0]});Q43=makeQuery(id+"F8.imprint","IMPRINT",FACE,{"disambiguationData":[TD([[makeQuery(id+"F8.imprint","IMPRINT",EDGE,{"disambiguationData":[TD([[subQ2,-1.0]])],"derivedFrom":subQ1}),-1.0]])]});}
            var Q44;
            {var subQ0=sQuery(id+"F8.wireOp",EDGE,"E30");var subQ1=sQuery(id+"F8.wireOp",EDGE,"E29");var subQ2=makeQuery(id+"F8.imprint","INTERSECT",VERTEX,{"disambiguationData":[OD(3.0)],"derivedFrom":[subQ1,subQ0]});Q44=makeQuery(id+"F8.imprint","IMPRINT",FACE,{"disambiguationData":[TD([[makeQuery(id+"F8.imprint","IMPRINT",EDGE,{"disambiguationData":[TD([[subQ2,-1.0]])],"derivedFrom":subQ1}),1.0]])]});}
            var Q45;
            {var subQ0=sQuery(id+"F8.wireOp",EDGE,"E42");var subQ1=sQuery(id+"F8.wireOp",EDGE,"E29");var subQ2=makeQuery(id+"F8.imprint","INTERSECT",VERTEX,{"derivedFrom":[subQ1,subQ0]});Q45=makeQuery(id+"F8.imprint","IMPRINT",FACE,{"disambiguationData":[TD([[makeQuery(id+"F8.imprint","IMPRINT",EDGE,{"disambiguationData":[TD([[subQ2,1.0]])],"derivedFrom":subQ1}),-1.0]])]});}
            var Q46;
            {var subQ0=sQuery(id+"F8.wireOp",EDGE,"E40");var subQ1=sQuery(id+"F8.wireOp",EDGE,"E29");var subQ2=makeQuery(id+"F8.imprint","INTERSECT",VERTEX,{"derivedFrom":[subQ1,subQ0]});Q46=makeQuery(id+"F8.imprint","IMPRINT",FACE,{"disambiguationData":[TD([[makeQuery(id+"F8.imprint","IMPRINT",EDGE,{"disambiguationData":[TD([[subQ2,1.0]])],"derivedFrom":subQ1}),-1.0]])]});}
            var Q47;
            {var subQ0=sQuery(id+"F8.wireOp",EDGE,"E41");var subQ1=sQuery(id+"F8.wireOp",EDGE,"E29");var subQ2=makeQuery(id+"F8.imprint","INTERSECT",VERTEX,{"derivedFrom":[subQ1,subQ0]});Q47=makeQuery(id+"F8.imprint","IMPRINT",FACE,{"disambiguationData":[TD([[makeQuery(id+"F8.imprint","IMPRINT",EDGE,{"disambiguationData":[TD([[subQ2,1.0]])],"derivedFrom":subQ1}),-1.0]])]});}
            var Q48;
            {var subQ0=sQuery(id+"F8.wireOp",EDGE,"E43");var subQ1=sQuery(id+"F8.wireOp",EDGE,"E29");var subQ2=makeQuery(id+"F8.imprint","INTERSECT",VERTEX,{"derivedFrom":[subQ1,subQ0]});Q48=makeQuery(id+"F8.imprint","IMPRINT",FACE,{"disambiguationData":[TD([[makeQuery(id+"F8.imprint","IMPRINT",EDGE,{"disambiguationData":[TD([[subQ2,-1.0]])],"derivedFrom":subQ1}),-1.0]])]});}
            var Q49;
            {var subQ0=sQuery(id+"F8.wireOp",EDGE,"E43");var subQ1=sQuery(id+"F8.wireOp",EDGE,"E29");var subQ2=makeQuery(id+"F8.imprint","INTERSECT",VERTEX,{"derivedFrom":[subQ1,subQ0]});Q49=makeQuery(id+"F8.imprint","IMPRINT",FACE,{"disambiguationData":[TD([[makeQuery(id+"F8.imprint","IMPRINT",EDGE,{"disambiguationData":[TD([[subQ2,1.0]])],"derivedFrom":subQ1}),-1.0]])]});}
            var Q50;
            {var subQ1=sQuery(id+"F8.wireOp",EDGE,"E31.bottom");var subQ18=sQuery(id+"F8.wireOp",EDGE,"E29");var subQ23=makeQuery(id+"F8.imprint","INTERSECT",VERTEX,{"disambiguationData":[OD(0.0)],"derivedFrom":[subQ18,subQ1]});Q50=makeQuery(id+"F8.imprint","IMPRINT",FACE,{"disambiguationData":[TD([[makeQuery(id+"F8.imprint","IMPRINT",EDGE,{"disambiguationData":[TD([[subQ23,-1.0]])],"derivedFrom":subQ18}),-1.0]])]});}
            var Q51;
            {var subQ0=sQuery(id+"F8.wireOp",EDGE,"E46");var subQ1=sQuery(id+"F8.wireOp",EDGE,"E29");var subQ2=makeQuery(id+"F8.imprint","INTERSECT",VERTEX,{"derivedFrom":[subQ1,subQ0]});Q51=makeQuery(id+"F8.imprint","IMPRINT",FACE,{"disambiguationData":[TD([[makeQuery(id+"F8.imprint","IMPRINT",EDGE,{"disambiguationData":[TD([[subQ2,-1.0]])],"derivedFrom":subQ1}),-1.0]])]});}
            var Q52;
            {var subQ0=sQuery(id+"F8.wireOp",EDGE,"E51");var subQ1=sQuery(id+"F8.wireOp",EDGE,"E30");var subQ2=makeQuery(id+"F8.imprint","INTERSECT",VERTEX,{"derivedFrom":[subQ1,subQ0]});Q52=makeQuery(id+"F8.imprint","IMPRINT",FACE,{"disambiguationData":[TD([[makeQuery(id+"F8.imprint","IMPRINT",EDGE,{"disambiguationData":[TD([[subQ2,-1.0]])],"derivedFrom":subQ1}),-1.0]])]});}
            var Q53;
            {var subQ0=sQuery(id+"F8.wireOp",EDGE,"E50");var subQ1=sQuery(id+"F8.wireOp",EDGE,"E30");var subQ2=makeQuery(id+"F8.imprint","INTERSECT",VERTEX,{"derivedFrom":[subQ1,subQ0]});Q53=makeQuery(id+"F8.imprint","IMPRINT",FACE,{"disambiguationData":[TD([[makeQuery(id+"F8.imprint","IMPRINT",EDGE,{"disambiguationData":[TD([[subQ2,-1.0]])],"derivedFrom":subQ1}),-1.0]])]});}
            var Q54;
            {var subQ1=sQuery(id+"F8.wireOp",EDGE,"E30");var subQ8=sQuery(id+"F8.wireOp",EDGE,"E31.right");var subQ11=makeQuery(id+"F8.imprint","INTERSECT",VERTEX,{"derivedFrom":[subQ1,subQ8]});Q54=makeQuery(id+"F8.imprint","IMPRINT",FACE,{"disambiguationData":[TD([[makeQuery(id+"F8.imprint","IMPRINT",EDGE,{"disambiguationData":[TD([[subQ11,-1.0]])],"derivedFrom":subQ1}),-1.0]])]});}
            var Q55;
            {var subQ0=sQuery(id+"F8.wireOp",EDGE,"E49");var subQ1=sQuery(id+"F8.wireOp",EDGE,"E30");var subQ2=makeQuery(id+"F8.imprint","INTERSECT",VERTEX,{"derivedFrom":[subQ1,subQ0]});Q55=makeQuery(id+"F8.imprint","IMPRINT",FACE,{"disambiguationData":[TD([[makeQuery(id+"F8.imprint","IMPRINT",EDGE,{"disambiguationData":[TD([[subQ2,-1.0]])],"derivedFrom":subQ1}),-1.0]])]});}
            var Q56;
            {var subQ7=sQuery(id+"F8.wireOp",EDGE,"E47");var subQ8=sQuery(id+"F8.wireOp",EDGE,"E30");var subQ9=makeQuery(id+"F8.imprint","INTERSECT",VERTEX,{"derivedFrom":[subQ8,subQ7]});Q56=makeQuery(id+"F8.imprint","IMPRINT",FACE,{"disambiguationData":[TD([[makeQuery(id+"F8.imprint","IMPRINT",EDGE,{"disambiguationData":[TD([[subQ9,-1.0]])],"derivedFrom":subQ8}),-1.0]])]});}
            var Q57;
            {var subQ0=sQuery(id+"F8.wireOp",EDGE,"E46");var subQ1=sQuery(id+"F8.wireOp",EDGE,"E30");var subQ2=makeQuery(id+"F8.imprint","INTERSECT",VERTEX,{"derivedFrom":[subQ1,subQ0]});Q57=makeQuery(id+"F8.imprint","IMPRINT",FACE,{"disambiguationData":[TD([[makeQuery(id+"F8.imprint","IMPRINT",EDGE,{"disambiguationData":[TD([[subQ2,-1.0]])],"derivedFrom":subQ1}),-1.0]])]});}
            var Q58;
            {var subQ0=sQuery(id+"F8.wireOp",EDGE,"E52");var subQ1=sQuery(id+"F8.wireOp",EDGE,"E29");var subQ2=makeQuery(id+"F8.imprint","INTERSECT",VERTEX,{"derivedFrom":[subQ1,subQ0]});Q58=makeQuery(id+"F8.imprint","IMPRINT",FACE,{"disambiguationData":[TD([[makeQuery(id+"F8.imprint","IMPRINT",EDGE,{"disambiguationData":[TD([[subQ2,1.0]])],"derivedFrom":subQ1}),-1.0]])]});}
            extrude(context, id + "F9", {"entities" : qUnion([Q0, Q1, Q2, Q3, Q4, Q5, Q6, Q7, Q8, Q9, Q10, Q11, Q12, Q13, Q14, Q15, Q16, Q17, Q18, Q19, Q20, Q21, Q22, Q23, Q24, Q25, Q26, Q27, Q28, Q29, Q30, Q31, Q32, Q33, Q34, Q35, Q36, Q37, Q38, Q39, Q40, Q41, Q42, Q43, Q44, Q45, Q46, Q47, Q48, Q49, Q50, Q51, Q52, Q53, Q54, Q55, Q56, Q57, Q58]), "depth" : 1 * mm});
        }
        {
            var Q0;
            Q0=makeQuery(id+"F9.opExtrude","CAP_FACE",FACE,{"disambiguationData":[OSD([sQuery(id+"F8.wireOp",EDGE,"E29"),sQuery(id+"F8.wireOp",EDGE,"E30"),sQuery(id+"F8.wireOp",EDGE,"E31.bottom")])],"isStart":false});
            var sketch = newSketch(context, id + "F10", { "sketchPlane" : qUnion([Q0])});
            skLineSegment(sketch, "E53.0", {"start": v(31.76, 16.35) * mm, "end": v(38.2, 16.35) * mm});
            skLineSegment(sketch, "E54.0", {"start": v(31.76, 16.35) * mm, "end": v(31.76, 15.33) * mm});
            skLineSegment(sketch, "E55.0", {"start": v(31.76, 15.33) * mm, "end": v(38.2, 15.33) * mm});
            skLineSegment(sketch, "E56.0", {"start": v(38.2, 16.35) * mm, "end": v(38.2, 15.33) * mm});
            skLineSegment(sketch, "E57", {"start": v(31.76, 16.25) * mm, "end": v(38.2, 16.25) * mm});
            skSolve(sketch);
        }
        {
            var Q0;
            {var subQ0=sQuery(id+"F10.wireOp",EDGE,"E55.0");Q0=makeQuery(id+"F10.imprint","IMPRINT",FACE,{"disambiguationData":[TD([[makeQuery(id+"F10.imprint","IMPRINT",EDGE,{"derivedFrom":subQ0}),1.0]])]});}
            extrude(context, id + "F11", {"entities" : qUnion([Q0]), "operationType" : NewBodyOperationType.REMOVE, "oppositeDirection" : true, "depth" : 1 * mm});
        }
        {
            var Q0;
            Q0=makeQuery(id+"F4.opExtrude","SWEPT_EDGE",EDGE,{"disambiguationData":[OSD([sQuery(id+"F3.wireOp",EDGE,"E21"),sQuery(id+"F3.wireOp",EDGE,"E28.bottom"),sQuery(id+"F3.wireOp",EDGE,"E10")])]});
            fillet(context, id + "F12", {"entities" : qUnion([Q0]), "radius" : 5 * mm, "tangentPropagation" : true, "allowEdgeOverflow" : false});
        }
        {
            var Q0;
            Q0=makeQuery(id+"F9.opExtrude","SWEPT_BODY",BODY,{"disambiguationData":[OSD([sQuery(id+"F8.wireOp",EDGE,"E29"),sQuery(id+"F8.wireOp",EDGE,"E30"),sQuery(id+"F8.wireOp",EDGE,"E31.bottom")])]});
            var Q1;
            Q1=sQuery(id+"F8.wireOp",EDGE,"E31.bottom");
            transform(context, id + "F13", {"entities" : qUnion([Q0]), "transformType" : TransformType.TRANSLATION_DISTANCE, "transformDirection" : qUnion([Q1]), "distance" : 8 * mm, "oppositeDirection" : true, "makeCopy" : false});
        }
    });
